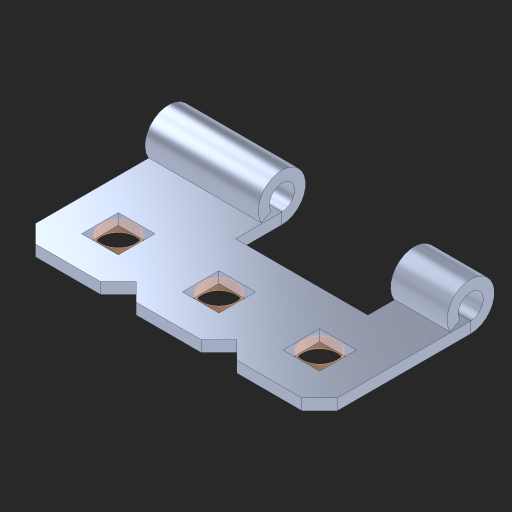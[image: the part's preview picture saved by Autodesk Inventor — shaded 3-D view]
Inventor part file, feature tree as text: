
AUTODESK INVENTOR PART (.ipt)
format: ipt  version: 2023 (Build 270158000, 158)  size: 206,336 bytes
history: native  units: in
note: dims shown in document units (in); Inventor stores cm internally (conversion verified against a paired STEP export)
features: other x5, extrude x4, sketch x2, pattern_linear x1, imported_body x1
ambient origin geometry x8: Origin, YZ Plane, XZ Plane, XY Plane, X Axis, Y Axis, Z Axis, Center Point
bodies: Body1 (feature_tree), Body2 (feature_tree), Body3 (feature_tree), Body4 (feature_tree)
feature tree (13):
  other  "Cut-Extrude3"
  other  "Top"
  pattern_linear  "Rectangular Pattern2"  Spacing1=0.5in  [1 undecoded]
  extrude  "Extrusion1"  Depth=1.0in
  imported_body  "Base1"
  sketch  "Sketch4"  dims[d30=0.172in]
  other  "Srf6"
  other  "Srf7"
  other  "Srf8"
  sketch  "Sketch5"  dims[d31=0.055in d32=0.0in d35=0.5in d36=1.0in d37=0.0in]
  extrude  "ExtrusionSrf6"  TaperAngle=0.0deg  [1 undecoded]
  extrude  "ExtrusionSrf7"  [1 undecoded]
  extrude  "ExtrusionSrf8"  [1 undecoded]
note: 4 required parameter values undecoded (feature->parameter linkage not recoverable at this tier; creation-order binding heuristic only, values carry confidence <= 0.55)
